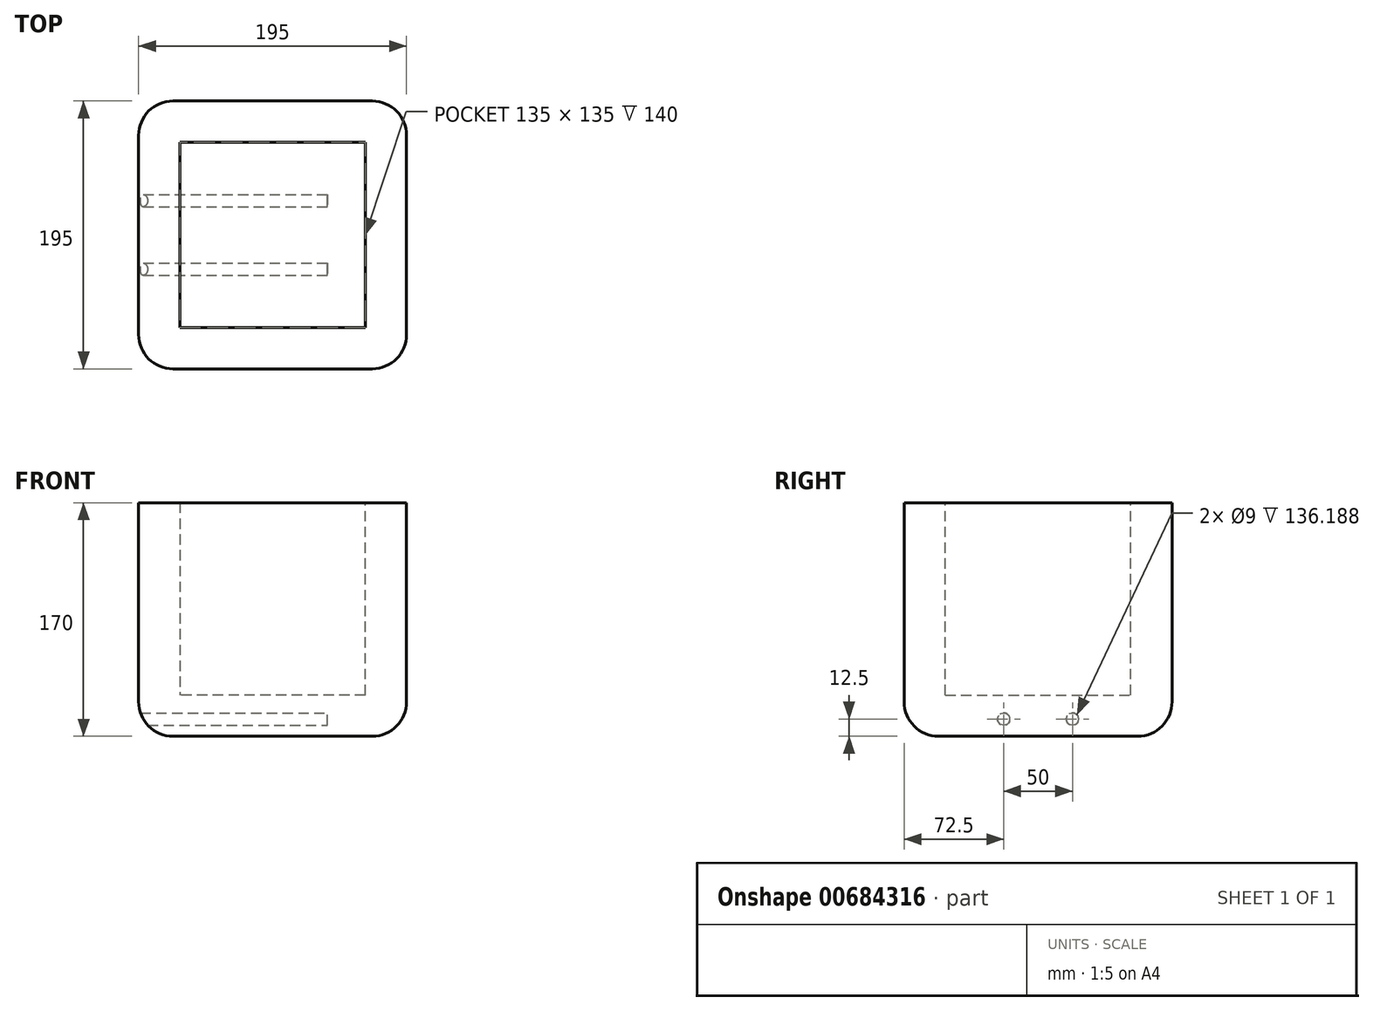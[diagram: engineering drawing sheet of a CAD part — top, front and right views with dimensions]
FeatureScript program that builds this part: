
annotation { "Feature Type Name" : "Feature", "Feature Type Description" : "" }
export const myFeature = defineFeature(function(context is Context, id is Id, definition is map)
    precondition{}
    {
        {
            var Q0;
            Q0=qCreatedBy(makeId("Top.planeOp"),FACE);
            var sketch = newSketch(context, id + "F0", { "sketchPlane" : qUnion([Q0])});
            skLineSegment(sketch, "E0.bottom", {"start": v(97.5, 97.5) * mm, "end": v(-97.5, 97.5) * mm});
            skLineSegment(sketch, "E0.top", {"start": v(97.5, -97.5) * mm, "end": v(-97.5, -97.5) * mm});
            skLineSegment(sketch, "E0.left", {"start": v(97.5, 97.5) * mm, "end": v(97.5, -97.5) * mm});
            skLineSegment(sketch, "E0.right", {"start": v(-97.5, 97.5) * mm, "end": v(-97.5, -97.5) * mm});
            skPoint(sketch, "E0.middle", {"position": v(0, 0) * mm});
            skSolve(sketch);
        }
        {
            var Q0;
            Q0=makeQuery(id+"F0.imprint","IMPRINT",FACE,{"disambiguationData":[TD([[makeQuery(id+"F0.imprint","IMPRINT",EDGE,{"derivedFrom":sQuery(id+"F0.wireOp",EDGE,"E0.bottom")}),1.0]])]});
            extrude(context, id + "F1", {"entities" : qUnion([Q0]), "depth" : 170 * mm, "offsetDistance" : 25 * mm});
        }
        {
            var Q0;
            Q0=qCreatedBy(makeId("Right.planeOp"),FACE);
            var sketch = newSketch(context, id + "F2", { "sketchPlane" : qUnion([Q0])});
            skCircle(sketch, "E1", {"center": v(-25, 12.5) * mm, "radius": 4.5 * mm});
            skLineSegment(sketch, "E2", {"start": v(0, 0) * mm, "end": v(0, 22.8) * mm, "construction": true});
            skCircle(sketch, "E3.MirrorC", {"center": v(25, 12.5) * mm, "radius": 4.5 * mm});
            skSolve(sketch);
        }
        {
            var Q0;
            Q0=makeQuery(id+"F1.opExtrude","CAP_FACE",FACE,{"disambiguationData":[OSD([sQuery(id+"F0.wireOp",EDGE,"E0.bottom"),sQuery(id+"F0.wireOp",EDGE,"E0.top"),sQuery(id+"F0.wireOp",EDGE,"E0.left"),sQuery(id+"F0.wireOp",EDGE,"E0.right")])],"isStart":true});
            var Q1;
            Q1=makeQuery(id+"F1.opExtrude","SWEPT_EDGE",EDGE,{"disambiguationData":[OSD([sQuery(id+"F0.wireOp",EDGE,"E0.bottom"),sQuery(id+"F0.wireOp",EDGE,"E0.left")])]});
            var Q2;
            Q2=makeQuery(id+"F1.opExtrude","SWEPT_EDGE",EDGE,{"disambiguationData":[OSD([sQuery(id+"F0.wireOp",EDGE,"E0.bottom"),sQuery(id+"F0.wireOp",EDGE,"E0.right")])]});
            var Q3;
            Q3=makeQuery(id+"F1.opExtrude","SWEPT_EDGE",EDGE,{"disambiguationData":[OSD([sQuery(id+"F0.wireOp",EDGE,"E0.top"),sQuery(id+"F0.wireOp",EDGE,"E0.right")])]});
            var Q4;
            Q4=makeQuery(id+"F1.opExtrude","SWEPT_EDGE",EDGE,{"disambiguationData":[OSD([sQuery(id+"F0.wireOp",EDGE,"E0.top"),sQuery(id+"F0.wireOp",EDGE,"E0.left")])]});
            fillet(context, id + "F3", {"entities" : qUnion([Q0, Q1, Q2, Q3, Q4]), "radius" : 25 * mm, "tangentPropagation" : true, "allowEdgeOverflow" : false});
        }
        {
            var Q0;
            Q0=makeQuery(id+"F1.opExtrude","CAP_FACE",FACE,{"disambiguationData":[OSD([sQuery(id+"F0.wireOp",EDGE,"E0.bottom"),sQuery(id+"F0.wireOp",EDGE,"E0.top"),sQuery(id+"F0.wireOp",EDGE,"E0.left"),sQuery(id+"F0.wireOp",EDGE,"E0.right")])],"isStart":false});
            shell(context, id + "F4", {"entities" : qUnion([Q0]), "thickness" : 30 * mm});
        }
        {
            var Q0;
            Q0 = qSketchRegion(id + "F2", true);
            extrude(context, id + "F5", {"entities" : qUnion([Q0]), "operationType" : NewBodyOperationType.REMOVE, "oppositeDirection" : true, "depth" : 195 * mm, "offsetDistance" : 25 * mm});
        }
        {
            var Q0;
            Q0 = qSketchRegion(id + "F2", true);
            extrude(context, id + "F6", {"entities" : qUnion([Q0]), "operationType" : NewBodyOperationType.REMOVE, "depth" : 40 * mm, "offsetDistance" : 25 * mm});
        }
    });
